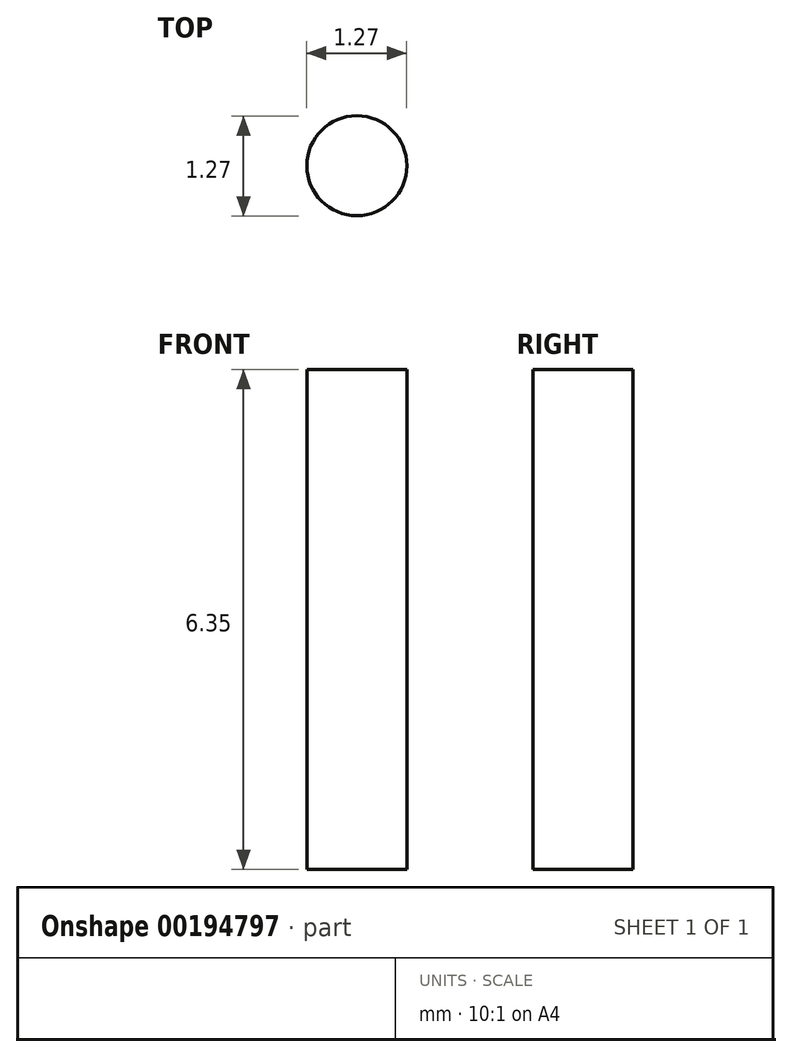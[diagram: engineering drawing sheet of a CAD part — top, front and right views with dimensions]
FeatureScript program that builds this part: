
annotation { "Feature Type Name" : "Feature", "Feature Type Description" : "" }
export const myFeature = defineFeature(function(context is Context, id is Id, definition is map)
    precondition{}
    {
        {
            var Q0;
            Q0=qCreatedBy(makeId("Top.planeOp"),FACE);
            var sketch = newSketch(context, id + "F0", { "sketchPlane" : qUnion([Q0])});
            skCircle(sketch, "E0", {"center": v(-86.17, -100.4) * mm, "radius": 0.64 * mm});
            skSolve(sketch);
        }
        {
            var Q0;
            Q0=makeQuery(id+"F0.imprint","IMPRINT",FACE,{"disambiguationData":[TD([[makeQuery(id+"F0.imprint","IMPRINT",EDGE,{"derivedFrom":sQuery(id+"F0.wireOp",EDGE,"E0")}),1.0]])]});
            extrude(context, id + "F1", {"entities" : qUnion([Q0]), "depth" : 6.35 * mm});
        }
    });
